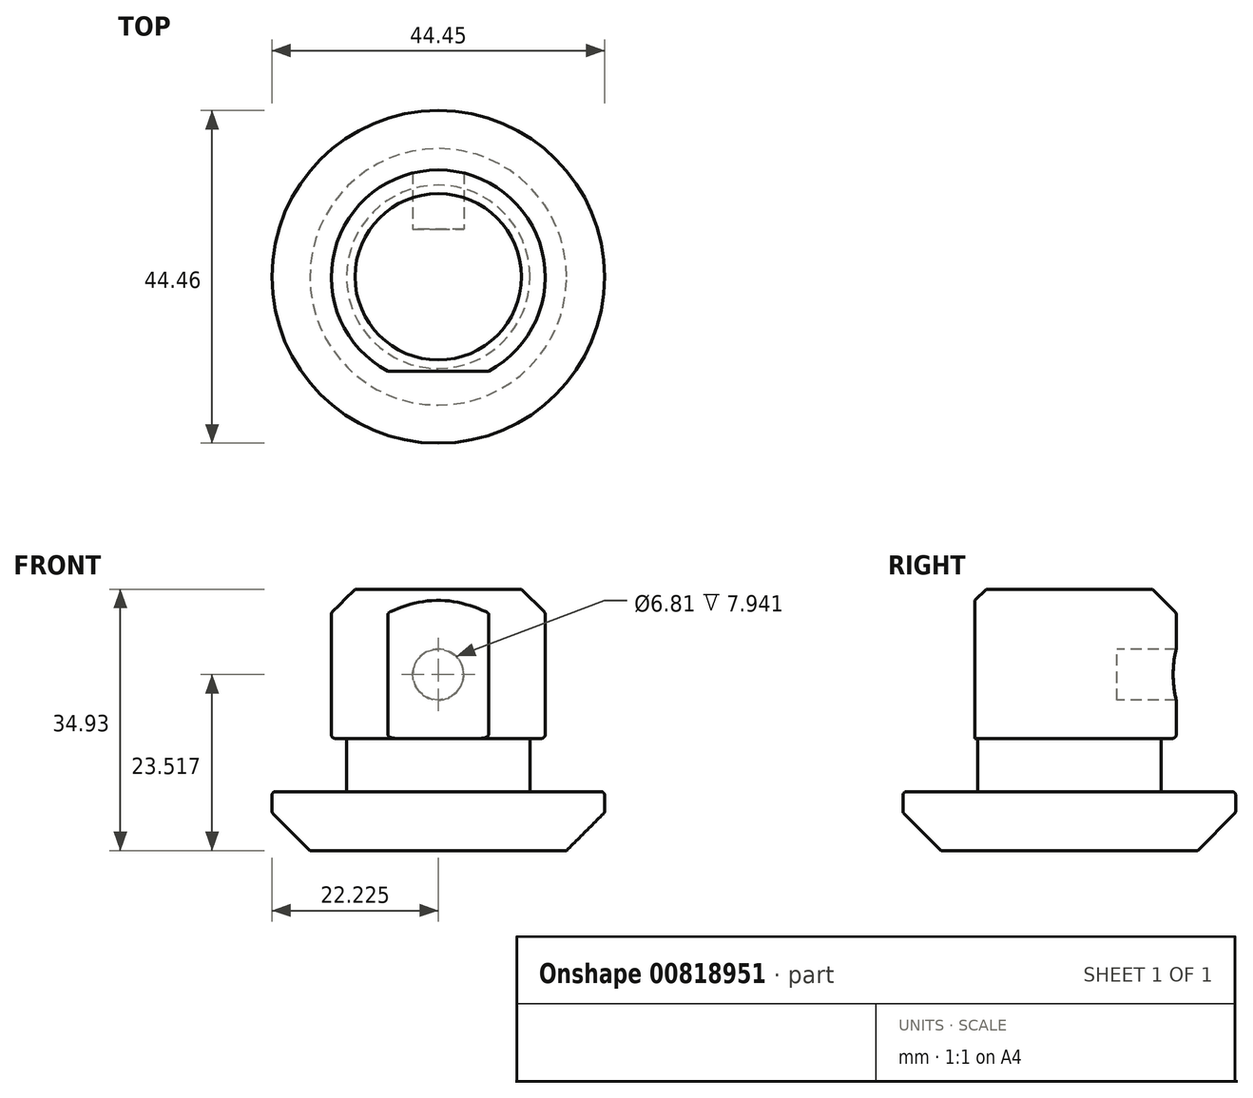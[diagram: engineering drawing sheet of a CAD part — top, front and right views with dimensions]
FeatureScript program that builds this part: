
annotation { "Feature Type Name" : "Feature", "Feature Type Description" : "" }
export const myFeature = defineFeature(function(context is Context, id is Id, definition is map)
    precondition{}
    {
        {
            var Q0;
            Q0=qCreatedBy(makeId("Front.planeOp"),FACE);
            var sketch = newSketch(context, id + "F0", { "sketchPlane" : qUnion([Q0])});
            skLineSegment(sketch, "E0", {"start": v(0, 0) * mm, "end": v(0, 7.87) * mm});
            skLineSegment(sketch, "E1", {"start": v(7.94, 34.93) * mm, "end": v(22.22, 34.93) * mm});
            skLineSegment(sketch, "E2", {"start": v(22.23, 34.93) * mm, "end": v(22.23, 0) * mm});
            skLineSegment(sketch, "E3", {"start": v(22.23, 0) * mm, "end": v(0, 0) * mm});
            skLineSegment(sketch, "E4", {"start": v(7.94, 34.93) * mm, "end": v(7.94, 14.99) * mm});
            skLineSegment(sketch, "E5", {"start": v(7.94, 14.99) * mm, "end": v(9.97, 14.99) * mm});
            skLineSegment(sketch, "E6", {"start": v(9.97, 7.87) * mm, "end": v(9.97, 14.99) * mm});
            skLineSegment(sketch, "E7", {"start": v(9.97, 7.87) * mm, "end": v(0, 7.87) * mm});
            skSolve(sketch);
        }
        {
            var Q0;
            Q0 = qSketchRegion(id + "F0", true);
            var Q1;
            Q1=sQuery(id+"F0.wireOp",EDGE,"E2");
            revolve(context, id + "F1", {"surfaceOperationType" : NewSurfaceOperationType.NEW, "entities" : qUnion([Q0]), "axis" : qUnion([Q1]), "revolveType" : RevolveType.FULL});
        }
        {
            var Q0;
            Q0=makeQuery(id+"F1.opRevolve","SWEPT_EDGE",EDGE,{"disambiguationData":[OSD([sQuery(id+"F0.wireOp",EDGE,"E0"),sQuery(id+"F0.wireOp",EDGE,"E3")])]});
            chamfer(context, id + "F2", {"entities" : qUnion([Q0]), "width" : 5.08 * mm, "tangentPropagation" : true});
        }
        {
            var Q0;
            Q0=makeQuery(id+"F1.opRevolve","SWEPT_EDGE",EDGE,{"disambiguationData":[OSD([sQuery(id+"F0.wireOp",EDGE,"E1"),sQuery(id+"F0.wireOp",EDGE,"E4")])]});
            chamfer(context, id + "F3", {"entities" : qUnion([Q0]), "width" : 3.17 * mm, "tangentPropagation" : true});
        }
        {
            var Q0;
            Q0=makeQuery(id+"F1.opRevolve","SWEPT_EDGE",EDGE,{"disambiguationData":[OSD([sQuery(id+"F0.wireOp",EDGE,"E4"),sQuery(id+"F0.wireOp",EDGE,"E5")])]});
            var Q1;
            Q1=makeQuery(id+"F1.opRevolve","SWEPT_FACE",FACE,{"disambiguationData":[OSD([sQuery(id+"F0.wireOp",EDGE,"E4")])]});
            var Q2;
            Q2=makeQuery(id+"F1.opRevolve","SWEPT_FACE",FACE,{"disambiguationData":[OSD([sQuery(id+"F0.wireOp",EDGE,"E0")])]});
            var Q3;
            Q3=makeQuery(id+"F1.opRevolve","SWEPT_EDGE",EDGE,{"disambiguationData":[OSD([sQuery(id+"F0.wireOp",EDGE,"E0"),sQuery(id+"F0.wireOp",EDGE,"E7")])]});
            fillet(context, id + "F4", {"entities" : qUnion([Q0, Q1, Q2, Q3]), "radius" : 0.5 * mm, "tangentPropagation" : true, "allowEdgeOverflow" : false});
        }
        {
            var Q0;
            Q0=qCreatedBy(makeId("Front.planeOp"),FACE);
            cPlane(context, id + "F5", {"entities" : qUnion([Q0]), "cplaneType" : CPlaneType.OFFSET, "offset" : 6.35 * mm, "oppositeDirection" : true, "width" : 152.4 * mm, "height" : 152.4 * mm});
        }
        {
            var Q0;
            Q0=qCreatedBy(id+"F5.planeOp",FACE);
            var sketch = newSketch(context, id + "F6", { "sketchPlane" : qUnion([Q0])});
            skCircle(sketch, "E8", {"center": v(22.23, 23.52) * mm, "radius": 3.4 * mm});
            skLineSegment(sketch, "E9", {"start": v(22.23, 31.54) * mm, "end": v(22.23, 15.5) * mm, "construction": true});
            skSolve(sketch);
        }
        {
            var Q0;
            Q0 = qSketchRegion(id + "F6", true);
            extrude(context, id + "F7", {"entities" : qUnion([Q0]), "operationType" : NewBodyOperationType.REMOVE, "oppositeDirection" : true, "depth" : 25.4 * mm, "offsetDistance" : 4.76 * mm, "offsetOppositeDirection" : true});
        }
        {
            var Q0;
            Q0=qCreatedBy(makeId("Right.planeOp"),FACE);
            var sketch = newSketch(context, id + "F8", { "sketchPlane" : qUnion([Q0])});
            skLineSegment(sketch, "E10", {"start": v(-12.6, 14.35) * mm, "end": v(-12.6, 35.4) * mm});
            skLineSegment(sketch, "E11", {"start": v(-12.6, 35.4) * mm, "end": v(-19.98, 35.4) * mm});
            skLineSegment(sketch, "E12", {"start": v(-19.98, 35.4) * mm, "end": v(-19.98, 14.35) * mm});
            skLineSegment(sketch, "E13", {"start": v(-19.98, 14.35) * mm, "end": v(-12.6, 14.35) * mm});
            skSolve(sketch);
        }
        {
            var Q0;
            Q0 = qSketchRegion(id + "F8", true);
            extrude(context, id + "F9", {"entities" : qUnion([Q0]), "operationType" : NewBodyOperationType.REMOVE, "endBound" : BoundingType.THROUGH_ALL, "depth" : 25.4 * mm, "offsetDistance" : 25.4 * mm});
        }
    });
